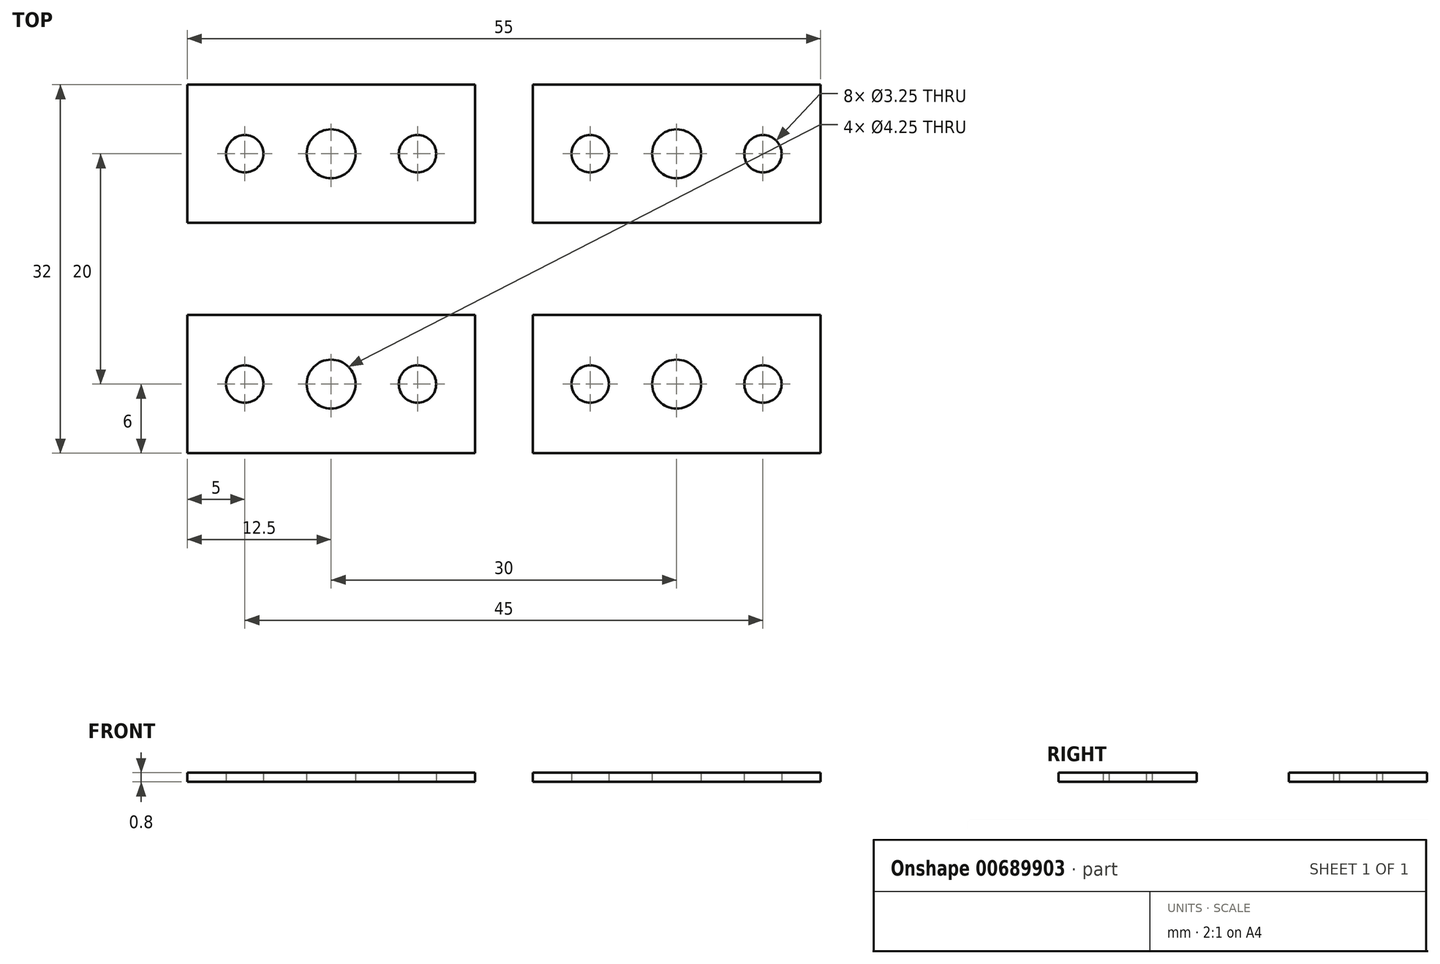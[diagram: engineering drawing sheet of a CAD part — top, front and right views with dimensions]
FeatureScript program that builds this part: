
annotation { "Feature Type Name" : "Feature", "Feature Type Description" : "" }
export const myFeature = defineFeature(function(context is Context, id is Id, definition is map)
    precondition{}
    {
        {
            var Q0;
            Q0=qCreatedBy(makeId("Top.planeOp"),FACE);
            var sketch = newSketch(context, id + "F0", { "sketchPlane" : qUnion([Q0])});
            skLineSegment(sketch, "E0.bottom", {"start": v(0, 0) * mm, "end": v(25, 0) * mm});
            skLineSegment(sketch, "E0.top", {"start": v(0, 12) * mm, "end": v(25, 12) * mm});
            skLineSegment(sketch, "E0.left", {"start": v(0, 0) * mm, "end": v(0, 12) * mm});
            skLineSegment(sketch, "E0.right", {"start": v(25, 0) * mm, "end": v(25, 12) * mm});
            skCircle(sketch, "E1", {"center": v(12.5, 6) * mm, "radius": 2.12 * mm});
            skCircle(sketch, "E2", {"center": v(5, 6) * mm, "radius": 1.63 * mm});
            skCircle(sketch, "E3", {"center": v(20, 6) * mm, "radius": 1.63 * mm});
            skLineSegment(sketch, "E4.0.1.0", {"start": v(25, 20) * mm, "end": v(25, 32) * mm});
            skLineSegment(sketch, "E4.0.1.1", {"start": v(0, 20) * mm, "end": v(25, 20) * mm});
            skCircle(sketch, "E4.0.1.2", {"center": v(12.5, 26) * mm, "radius": 2.12 * mm});
            skCircle(sketch, "E4.0.1.3", {"center": v(20, 26) * mm, "radius": 1.63 * mm});
            skCircle(sketch, "E4.0.1.4", {"center": v(5, 26) * mm, "radius": 1.63 * mm});
            skLineSegment(sketch, "E4.0.1.5", {"start": v(0, 20) * mm, "end": v(0, 32) * mm});
            skLineSegment(sketch, "E4.0.1.6", {"start": v(0, 32) * mm, "end": v(25, 32) * mm});
            skLineSegment(sketch, "E4.1.0.0", {"start": v(55, 0) * mm, "end": v(55, 12) * mm});
            skLineSegment(sketch, "E4.1.0.1", {"start": v(30, 0) * mm, "end": v(55, 0) * mm});
            skCircle(sketch, "E4.1.0.2", {"center": v(42.5, 6) * mm, "radius": 2.12 * mm});
            skCircle(sketch, "E4.1.0.3", {"center": v(50, 6) * mm, "radius": 1.63 * mm});
            skCircle(sketch, "E4.1.0.4", {"center": v(35, 6) * mm, "radius": 1.63 * mm});
            skLineSegment(sketch, "E4.1.0.5", {"start": v(30, 0) * mm, "end": v(30, 12) * mm});
            skLineSegment(sketch, "E4.1.0.6", {"start": v(30, 12) * mm, "end": v(55, 12) * mm});
            skLineSegment(sketch, "E4.1.1.0", {"start": v(55, 20) * mm, "end": v(55, 32) * mm});
            skLineSegment(sketch, "E4.1.1.1", {"start": v(30, 20) * mm, "end": v(55, 20) * mm});
            skCircle(sketch, "E4.1.1.2", {"center": v(42.5, 26) * mm, "radius": 2.12 * mm});
            skCircle(sketch, "E4.1.1.3", {"center": v(50, 26) * mm, "radius": 1.63 * mm});
            skCircle(sketch, "E4.1.1.4", {"center": v(35, 26) * mm, "radius": 1.63 * mm});
            skLineSegment(sketch, "E4.1.1.5", {"start": v(30, 20) * mm, "end": v(30, 32) * mm});
            skLineSegment(sketch, "E4.1.1.6", {"start": v(30, 32) * mm, "end": v(55, 32) * mm});
            skLineSegment(sketch, "E4.direction1", {"start": v(0, 0) * mm, "end": v(30, 0) * mm, "construction": true});
            skLineSegment(sketch, "E4.direction2", {"start": v(0, 0) * mm, "end": v(0, 20) * mm, "construction": true});
            skSolve(sketch);
        }
        {
            var Q0;
            Q0=makeQuery(id+"F0.imprint","IMPRINT",FACE,{"disambiguationData":[TD([[makeQuery(id+"F0.imprint","IMPRINT",EDGE,{"derivedFrom":sQuery(id+"F0.wireOp",EDGE,"E4.0.1.0")}),1.0]])]});
            var Q1;
            Q1=makeQuery(id+"F0.imprint","IMPRINT",FACE,{"disambiguationData":[TD([[makeQuery(id+"F0.imprint","IMPRINT",EDGE,{"derivedFrom":sQuery(id+"F0.wireOp",EDGE,"E4.1.1.0")}),1.0]])]});
            var Q2;
            Q2=makeQuery(id+"F0.imprint","IMPRINT",FACE,{"disambiguationData":[TD([[makeQuery(id+"F0.imprint","IMPRINT",EDGE,{"derivedFrom":sQuery(id+"F0.wireOp",EDGE,"E4.1.0.0")}),1.0]])]});
            var Q3;
            Q3=makeQuery(id+"F0.imprint","IMPRINT",FACE,{"disambiguationData":[TD([[makeQuery(id+"F0.imprint","IMPRINT",EDGE,{"derivedFrom":sQuery(id+"F0.wireOp",EDGE,"E0.bottom")}),1.0]])]});
            extrude(context, id + "F1", {"entities" : qUnion([Q0, Q1, Q2, Q3]), "depth" : 0.8 * mm, "offsetDistance" : 25 * mm});
        }
    });
